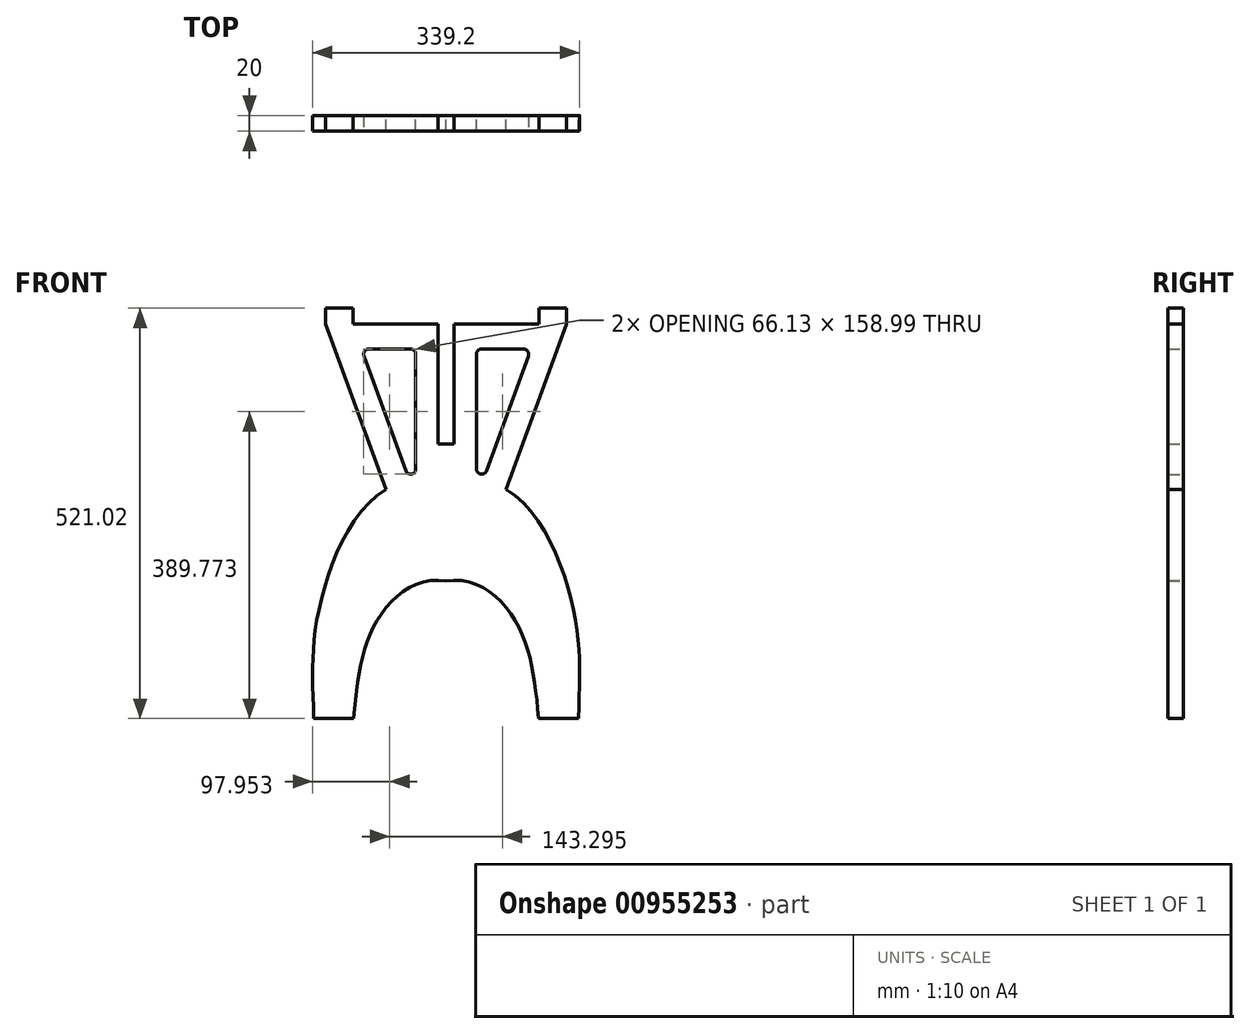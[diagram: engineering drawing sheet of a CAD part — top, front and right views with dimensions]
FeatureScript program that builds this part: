
annotation { "Feature Type Name" : "Feature", "Feature Type Description" : "" }
export const myFeature = defineFeature(function(context is Context, id is Id, definition is map)
    precondition{}
    {
        {
            var Q0;
            Q0=qCreatedBy(makeId("Front.planeOp"),FACE);
            var sketch = newSketch(context, id + "F0", { "sketchPlane" : qUnion([Q0])});
            skLineSegment(sketch, "E0", {"start": v(-10, 501.02) * mm, "end": v(-152.88, 501.02) * mm});
            skLineSegment(sketch, "E1", {"start": v(-152.88, 501.02) * mm, "end": v(-76.3, 290.6) * mm});
            skLineSegment(sketch, "E2", {"start": v(-10, 501.02) * mm, "end": v(-10, 348.62) * mm});
            skLineSegment(sketch, "E3", {"start": v(-10, 348.62) * mm, "end": v(0, 348.62) * mm});
            skLineSegment(sketch, "E4", {"start": v(0, 348.62) * mm, "end": v(0, 174.31) * mm});
            skLineSegment(sketch, "E5", {"start": v(-168.28, 0) * mm, "end": v(-117.48, 0) * mm});
            skPoint(sketch, "E6.orphan", {"position": v(0, 0) * mm});
            skFitSpline(sketch, "E7", {"points": [v(-168.28, 0) * mm, v(-162.77, 132.42) * mm, v(-76.3, 290.6) * mm], "startDerivative": vector(-8.33, 341.07) * mm, "endDerivative": vector(269.82, 154.86) * mm});
            skFitSpline(sketch, "E8", {"points": [v(-117.48, 0) * mm, v(-85.92, 127.41) * mm, v(0, 174.31) * mm], "startDerivative": vector(24.85, 274) * mm, "endDerivative": vector(231.76, -42.5) * mm});
            skSolve(sketch);
        }
        {
            var Q0;
            Q0=makeQuery(id+"F0.imprint","IMPRINT",FACE,{"disambiguationData":[TD([[makeQuery(id+"F0.imprint","IMPRINT",EDGE,{"derivedFrom":sQuery(id+"F0.wireOp",EDGE,"E0")}),1.0]])]});
            extrude(context, id + "F1", {"entities" : qUnion([Q0]), "depth" : 20 * mm, "offsetDistance" : 25 * mm});
        }
        {
            var Q0;
            Q0=makeQuery(id+"F0.imprint","IMPRINT",FACE,{"disambiguationData":[TD([[makeQuery(id+"F0.imprint","IMPRINT",EDGE,{"derivedFrom":sQuery(id+"F0.wireOp",EDGE,"E0")}),1.0]])]});
            var sketch = newSketch(context, id + "F2", { "sketchPlane" : qUnion([Q0])});
            skLineSegment(sketch, "E9.0", {"start": v(-38.58, 469.27) * mm, "end": v(-107.54, 469.27) * mm});
            skLineSegment(sketch, "E10.0", {"start": v(-38.58, 469.27) * mm, "end": v(-38.58, 279.81) * mm});
            skLineSegment(sketch, "E11.0", {"start": v(-107.54, 469.27) * mm, "end": v(-38.58, 279.81) * mm});
            skSolve(sketch);
        }
        {
            var Q0;
            Q0 = qSketchRegion(id + "F2", true);
            extrude(context, id + "F3", {"entities" : qUnion([Q0]), "operationType" : NewBodyOperationType.REMOVE, "depth" : 25 * mm, "offsetDistance" : 25 * mm});
        }
        {
            var Q0;
            Q0=makeQuery(id+"F1.opExtrude","SWEPT_FACE",FACE,{"disambiguationData":[OSD([sQuery(id+"F0.wireOp",EDGE,"E0")])]});
            var sketch = newSketch(context, id + "F4", { "sketchPlane" : qUnion([Q0])});
            skLineSegment(sketch, "E12.bottom", {"start": v(-152.88, 0) * mm, "end": v(-117.95, 0) * mm});
            skLineSegment(sketch, "E12.top", {"start": v(-152.88, -20) * mm, "end": v(-117.95, -20) * mm});
            skLineSegment(sketch, "E12.left", {"start": v(-152.88, 0) * mm, "end": v(-152.88, -20) * mm});
            skLineSegment(sketch, "E12.right", {"start": v(-117.95, 0) * mm, "end": v(-117.95, -20) * mm});
            skSolve(sketch);
        }
        {
            var Q0;
            Q0=makeQuery(id+"F4.imprint","IMPRINT",FACE,{"disambiguationData":[TD([[makeQuery(id+"F4.imprint","IMPRINT",EDGE,{"derivedFrom":sQuery(id+"F4.wireOp",EDGE,"E12.bottom")}),1.0]])]});
            extrude(context, id + "F5", {"entities" : qUnion([Q0]), "operationType" : NewBodyOperationType.ADD, "depth" : 20 * mm, "offsetDistance" : 25 * mm});
        }
        {
            var Q0;
            Q0=makeQuery(id+"F1.opExtrude","SWEPT_BODY",BODY,{"disambiguationData":[OSD([sQuery(id+"F0.wireOp",EDGE,"E0"),sQuery(id+"F0.wireOp",EDGE,"E1"),sQuery(id+"F0.wireOp",EDGE,"E2"),sQuery(id+"F0.wireOp",EDGE,"E3"),sQuery(id+"F0.wireOp",EDGE,"E4"),sQuery(id+"F0.wireOp",EDGE,"E5"),sQuery(id+"F0.wireOp",EDGE,"E7"),sQuery(id+"F0.wireOp",EDGE,"E8")])]});
            var Q1;
            Q1=qCreatedBy(makeId("Right.planeOp"),FACE);
            mirror(context, id + "F6", {"operationType" : NewBodyOperationType.ADD, "entities" : qUnion([Q0]), "mirrorPlane" : qUnion([Q1])});
        }
        {
            var Q0;
            Q0=makeQuery(id+"F3.boolean.opBoolean","COPY",EDGE,{"derivedFrom":makeQuery(id+"F3.opExtrude","SWEPT_EDGE",EDGE,{"disambiguationData":[OSD([sQuery(id+"F2.wireOp",EDGE,"E9.0"),sQuery(id+"F2.wireOp",EDGE,"E11.0")])]})});
            var Q1;
            Q1=makeQuery(id+"F3.boolean.opBoolean","COPY",EDGE,{"derivedFrom":makeQuery(id+"F3.opExtrude","SWEPT_EDGE",EDGE,{"disambiguationData":[OSD([sQuery(id+"F2.wireOp",EDGE,"E9.0"),sQuery(id+"F2.wireOp",EDGE,"E10.0")])]})});
            var Q2;
            Q2=makeQuery(id+"F3.boolean.opBoolean","COPY",EDGE,{"derivedFrom":makeQuery(id+"F3.opExtrude","SWEPT_EDGE",EDGE,{"disambiguationData":[OSD([sQuery(id+"F2.wireOp",EDGE,"E10.0"),sQuery(id+"F2.wireOp",EDGE,"E11.0")])]})});
            var Q3;
            Q3=makeQuery(id+"F6.opPattern","COPY",EDGE,{"derivedFrom":makeQuery(id+"F3.boolean.opBoolean","COPY",EDGE,{"derivedFrom":makeQuery(id+"F3.opExtrude","SWEPT_EDGE",EDGE,{"disambiguationData":[OSD([sQuery(id+"F2.wireOp",EDGE,"E10.0"),sQuery(id+"F2.wireOp",EDGE,"E11.0")])]})}),"instanceName":"1"});
            var Q4;
            Q4=makeQuery(id+"F6.opPattern","COPY",EDGE,{"derivedFrom":makeQuery(id+"F3.boolean.opBoolean","COPY",EDGE,{"derivedFrom":makeQuery(id+"F3.opExtrude","SWEPT_EDGE",EDGE,{"disambiguationData":[OSD([sQuery(id+"F2.wireOp",EDGE,"E9.0"),sQuery(id+"F2.wireOp",EDGE,"E10.0")])]})}),"instanceName":"1"});
            var Q5;
            Q5=makeQuery(id+"F6.opPattern","COPY",EDGE,{"derivedFrom":makeQuery(id+"F3.boolean.opBoolean","COPY",EDGE,{"derivedFrom":makeQuery(id+"F3.opExtrude","SWEPT_EDGE",EDGE,{"disambiguationData":[OSD([sQuery(id+"F2.wireOp",EDGE,"E9.0"),sQuery(id+"F2.wireOp",EDGE,"E11.0")])]})}),"instanceName":"1"});
            fillet(context, id + "F7", {"entities" : qUnion([Q0, Q1, Q2, Q3, Q4, Q5]), "radius" : 6.5 * mm, "tangentPropagation" : true, "allowEdgeOverflow" : false});
        }
    });
